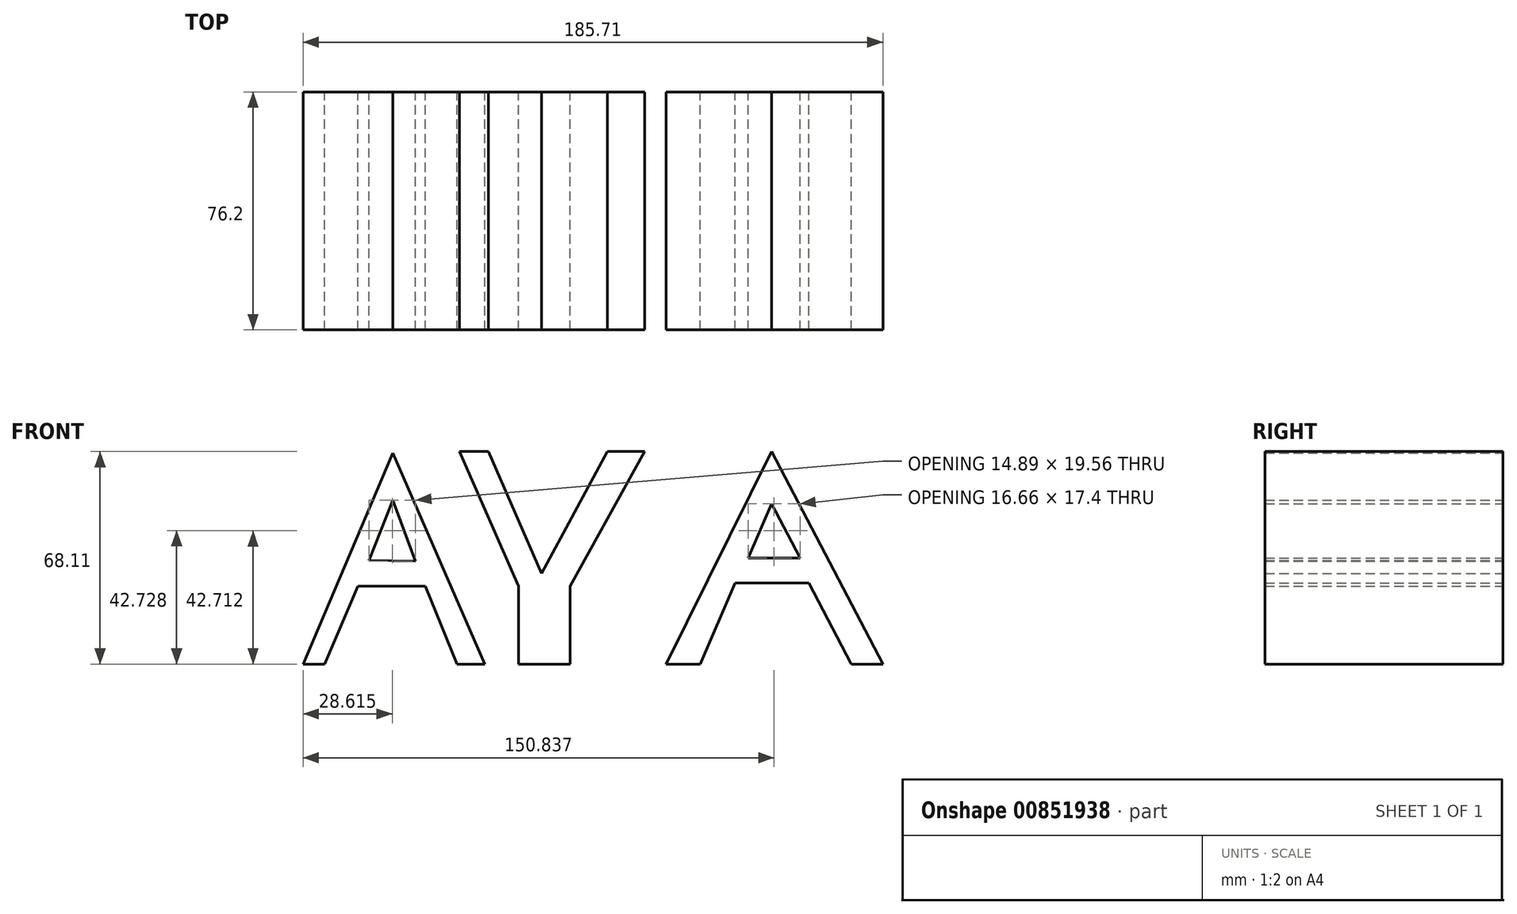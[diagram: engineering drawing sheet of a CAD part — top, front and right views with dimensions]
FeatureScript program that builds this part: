
annotation { "Feature Type Name" : "Feature", "Feature Type Description" : "" }
export const myFeature = defineFeature(function(context is Context, id is Id, definition is map)
    precondition{}
    {
        {
            var Q0;
            Q0=qCreatedBy(makeId("Front.planeOp"),FACE);
            var sketch = newSketch(context, id + "F0", { "sketchPlane" : qUnion([Q0])});
            skLineSegment(sketch, "E0", {"start": v(0, 0) * mm, "end": v(28.73, 67.62) * mm});
            skLineSegment(sketch, "E1", {"start": v(28.73, 67.62) * mm, "end": v(58.29, 0) * mm});
            skLineSegment(sketch, "E2", {"start": v(58.29, 0) * mm, "end": v(49.4, 0) * mm});
            skLineSegment(sketch, "E3", {"start": v(49.4, 0) * mm, "end": v(39.17, 24.95) * mm});
            skLineSegment(sketch, "E4", {"start": v(39.17, 24.95) * mm, "end": v(17.61, 24.95) * mm});
            skLineSegment(sketch, "E5", {"start": v(17.61, 24.95) * mm, "end": v(6.95, 0) * mm});
            skLineSegment(sketch, "E6", {"start": v(6.95, 0) * mm, "end": v(0, 0) * mm});
            skLineSegment(sketch, "E7", {"start": v(21.17, 33.17) * mm, "end": v(28.73, 52.5) * mm});
            skLineSegment(sketch, "E8", {"start": v(28.73, 52.5) * mm, "end": v(36.06, 32.95) * mm});
            skLineSegment(sketch, "E9", {"start": v(36.06, 32.95) * mm, "end": v(21.17, 33.17) * mm});
            skLineSegment(sketch, "E10", {"start": v(76.14, 0) * mm, "end": v(85.51, 0) * mm});
            skLineSegment(sketch, "E11", {"start": v(85.51, 0) * mm, "end": v(85.51, 24.95) * mm});
            skLineSegment(sketch, "E12", {"start": v(85.51, 24.95) * mm, "end": v(109.45, 68.1) * mm});
            skLineSegment(sketch, "E13", {"start": v(109.45, 68.1) * mm, "end": v(97.48, 68.1) * mm});
            skLineSegment(sketch, "E14", {"start": v(97.48, 68.1) * mm, "end": v(76.4, 29.07) * mm});
            skLineSegment(sketch, "E15", {"start": v(76.4, 29.07) * mm, "end": v(59.34, 68.1) * mm});
            skLineSegment(sketch, "E16", {"start": v(59.34, 68.1) * mm, "end": v(50.12, 68.1) * mm});
            skLineSegment(sketch, "E17", {"start": v(50.12, 68.1) * mm, "end": v(68.98, 24.95) * mm});
            skLineSegment(sketch, "E18", {"start": v(68.98, 24.95) * mm, "end": v(68.98, 0) * mm});
            skLineSegment(sketch, "E19", {"start": v(68.98, 0) * mm, "end": v(76.14, 0) * mm});
            skLineSegment(sketch, "E20", {"start": v(116.22, 0) * mm, "end": v(150.06, 68.1) * mm});
            skLineSegment(sketch, "E21", {"start": v(150.06, 68.1) * mm, "end": v(185.71, 0) * mm});
            skLineSegment(sketch, "E22", {"start": v(185.71, 0) * mm, "end": v(175.56, 0) * mm});
            skLineSegment(sketch, "E23", {"start": v(175.56, 0) * mm, "end": v(162.03, 25.94) * mm});
            skLineSegment(sketch, "E24", {"start": v(162.03, 25.94) * mm, "end": v(138.34, 25.94) * mm});
            skLineSegment(sketch, "E25", {"start": v(138.34, 25.94) * mm, "end": v(127.15, 0) * mm});
            skLineSegment(sketch, "E26", {"start": v(127.15, 0) * mm, "end": v(116.22, 0) * mm});
            skLineSegment(sketch, "E27", {"start": v(142.5, 34.01) * mm, "end": v(159.16, 34.01) * mm});
            skLineSegment(sketch, "E28", {"start": v(159.16, 34.01) * mm, "end": v(150.06, 51.41) * mm});
            skLineSegment(sketch, "E29", {"start": v(150.06, 51.41) * mm, "end": v(142.5, 34.01) * mm});
            skSolve(sketch);
        }
        {
            var Q0;
            Q0=makeQuery(id+"F0.imprint","IMPRINT",FACE,{"disambiguationData":[TD([[makeQuery(id+"F0.imprint","IMPRINT",EDGE,{"derivedFrom":sQuery(id+"F0.wireOp",EDGE,"E0")}),-1.0]])]});
            var Q1;
            Q1=makeQuery(id+"F0.imprint","IMPRINT",FACE,{"disambiguationData":[TD([[makeQuery(id+"F0.imprint","IMPRINT",EDGE,{"derivedFrom":sQuery(id+"F0.wireOp",EDGE,"E10")}),1.0]])]});
            var Q2;
            Q2=makeQuery(id+"F0.imprint","IMPRINT",FACE,{"disambiguationData":[TD([[makeQuery(id+"F0.imprint","IMPRINT",EDGE,{"derivedFrom":sQuery(id+"F0.wireOp",EDGE,"E20")}),-1.0]])]});
            extrude(context, id + "F1", {"entities" : qUnion([Q0, Q1, Q2]), "depth" : 76.2 * mm, "offsetDistance" : 25.4 * mm});
        }
    });
